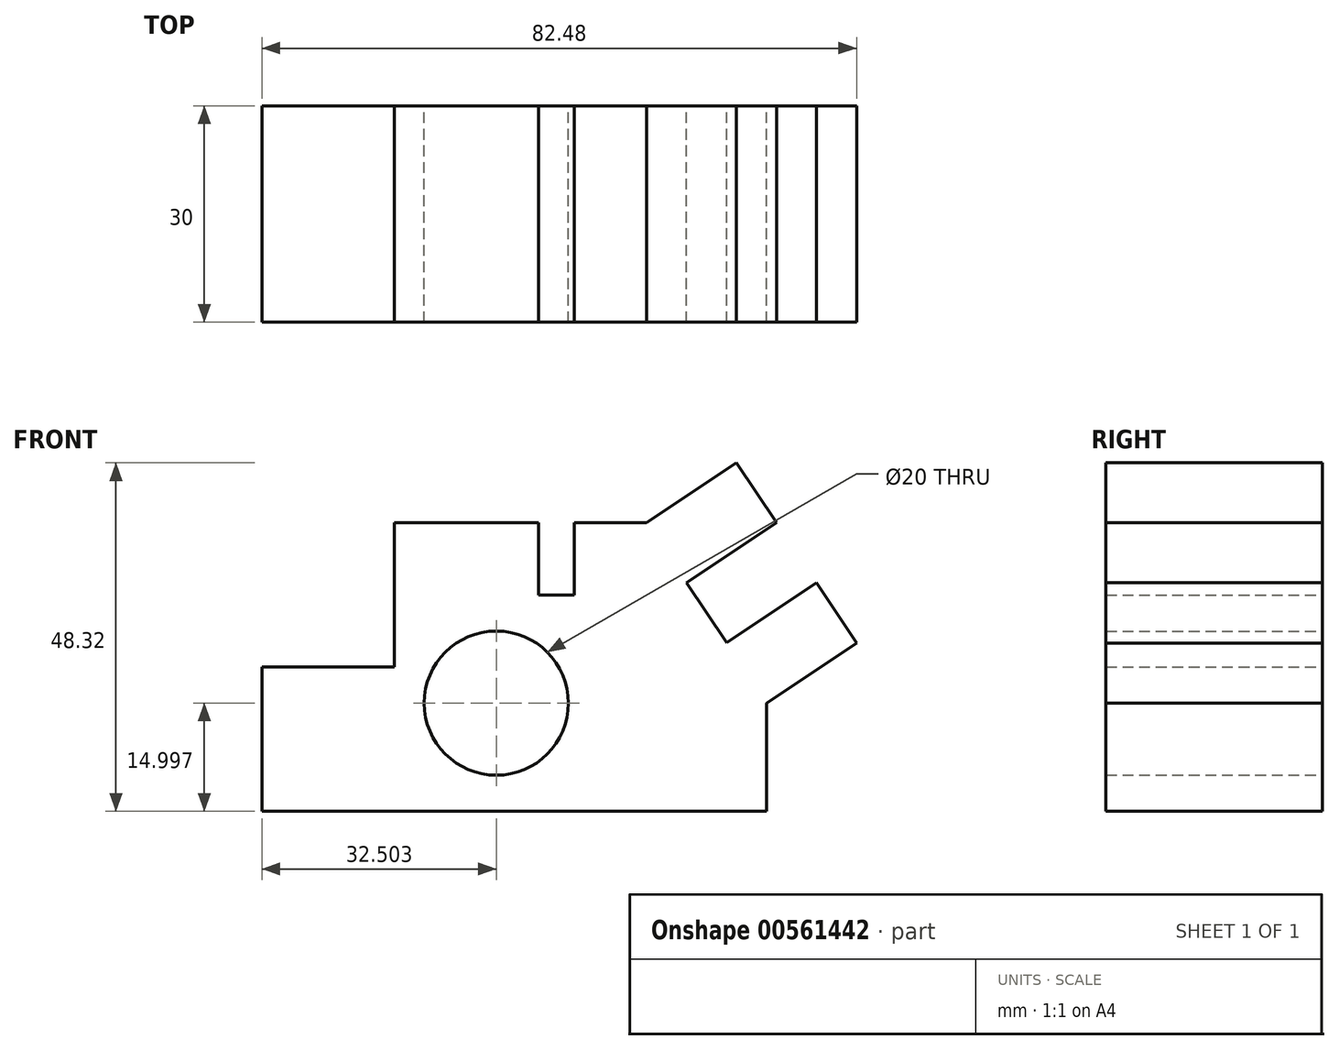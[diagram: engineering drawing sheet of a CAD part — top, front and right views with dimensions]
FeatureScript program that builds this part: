
annotation { "Feature Type Name" : "Feature", "Feature Type Description" : "" }
export const myFeature = defineFeature(function(context is Context, id is Id, definition is map)
    precondition{}
    {
        {
            var Q0;
            Q0=qCreatedBy(makeId("Front.planeOp"),FACE);
            var sketch = newSketch(context, id + "F0", { "sketchPlane" : qUnion([Q0])});
            skLineSegment(sketch, "E0", {"start": v(1.59, 21.44) * mm, "end": v(21.59, 21.44) * mm});
            skLineSegment(sketch, "E1", {"start": v(36.59, 21.44) * mm, "end": v(53.25, -3.56) * mm});
            skLineSegment(sketch, "E2", {"start": v(53.25, -3.56) * mm, "end": v(53.25, -18.56) * mm});
            skLineSegment(sketch, "E3", {"start": v(53.25, -18.56) * mm, "end": v(-16.75, -18.56) * mm});
            skLineSegment(sketch, "E4", {"start": v(-16.75, -18.56) * mm, "end": v(-16.75, 1.44) * mm});
            skLineSegment(sketch, "E5", {"start": v(-16.75, 1.44) * mm, "end": v(1.59, 1.44) * mm});
            skLineSegment(sketch, "E6", {"start": v(1.59, 1.44) * mm, "end": v(1.59, 21.44) * mm});
            skLineSegment(sketch, "E7", {"start": v(21.59, 21.44) * mm, "end": v(21.59, 11.44) * mm});
            skLineSegment(sketch, "E8", {"start": v(21.59, 11.44) * mm, "end": v(26.59, 11.44) * mm});
            skLineSegment(sketch, "E9", {"start": v(26.59, 11.44) * mm, "end": v(26.59, 21.44) * mm});
            skLineSegment(sketch, "E10.trimOffspring", {"start": v(26.59, 21.44) * mm, "end": v(36.59, 21.44) * mm});
            skLineSegment(sketch, "E11", {"start": v(36.59, 21.44) * mm, "end": v(49.07, 29.76) * mm});
            skLineSegment(sketch, "E12", {"start": v(49.07, 29.76) * mm, "end": v(54.61, 21.44) * mm});
            skLineSegment(sketch, "E13", {"start": v(54.61, 21.44) * mm, "end": v(42.13, 13.12) * mm});
            skLineSegment(sketch, "E14", {"start": v(53.25, -3.56) * mm, "end": v(65.73, 4.76) * mm});
            skLineSegment(sketch, "E15", {"start": v(65.73, 4.76) * mm, "end": v(60.16, 13.12) * mm});
            skLineSegment(sketch, "E16", {"start": v(60.16, 13.12) * mm, "end": v(47.68, 4.8) * mm});
            skCircle(sketch, "E17", {"center": v(15.75, -3.56) * mm, "radius": 10 * mm});
            skSolve(sketch);
        }
        {
            var Q0;
            Q0=makeQuery(id+"F0.imprint","IMPRINT",FACE,{"disambiguationData":[TD([[makeQuery(id+"F0.imprint","IMPRINT",EDGE,{"derivedFrom":sQuery(id+"F0.wireOp",EDGE,"E0")}),-1.0]])]});
            var Q1;
            {var subQ0=sQuery(id+"F0.wireOp",EDGE,"E11");Q1=makeQuery(id+"F0.imprint","IMPRINT",FACE,{"disambiguationData":[TD([[makeQuery(id+"F0.imprint","IMPRINT",EDGE,{"derivedFrom":subQ0}),-1.0]])]});}
            var Q2;
            {var subQ0=sQuery(id+"F0.wireOp",EDGE,"E14");Q2=makeQuery(id+"F0.imprint","IMPRINT",FACE,{"disambiguationData":[TD([[makeQuery(id+"F0.imprint","IMPRINT",EDGE,{"derivedFrom":subQ0}),1.0]])]});}
            extrude(context, id + "F1", {"entities" : qUnion([Q0, Q1, Q2]), "depth" : 30 * mm, "offsetDistance" : 25 * mm});
        }
    });
